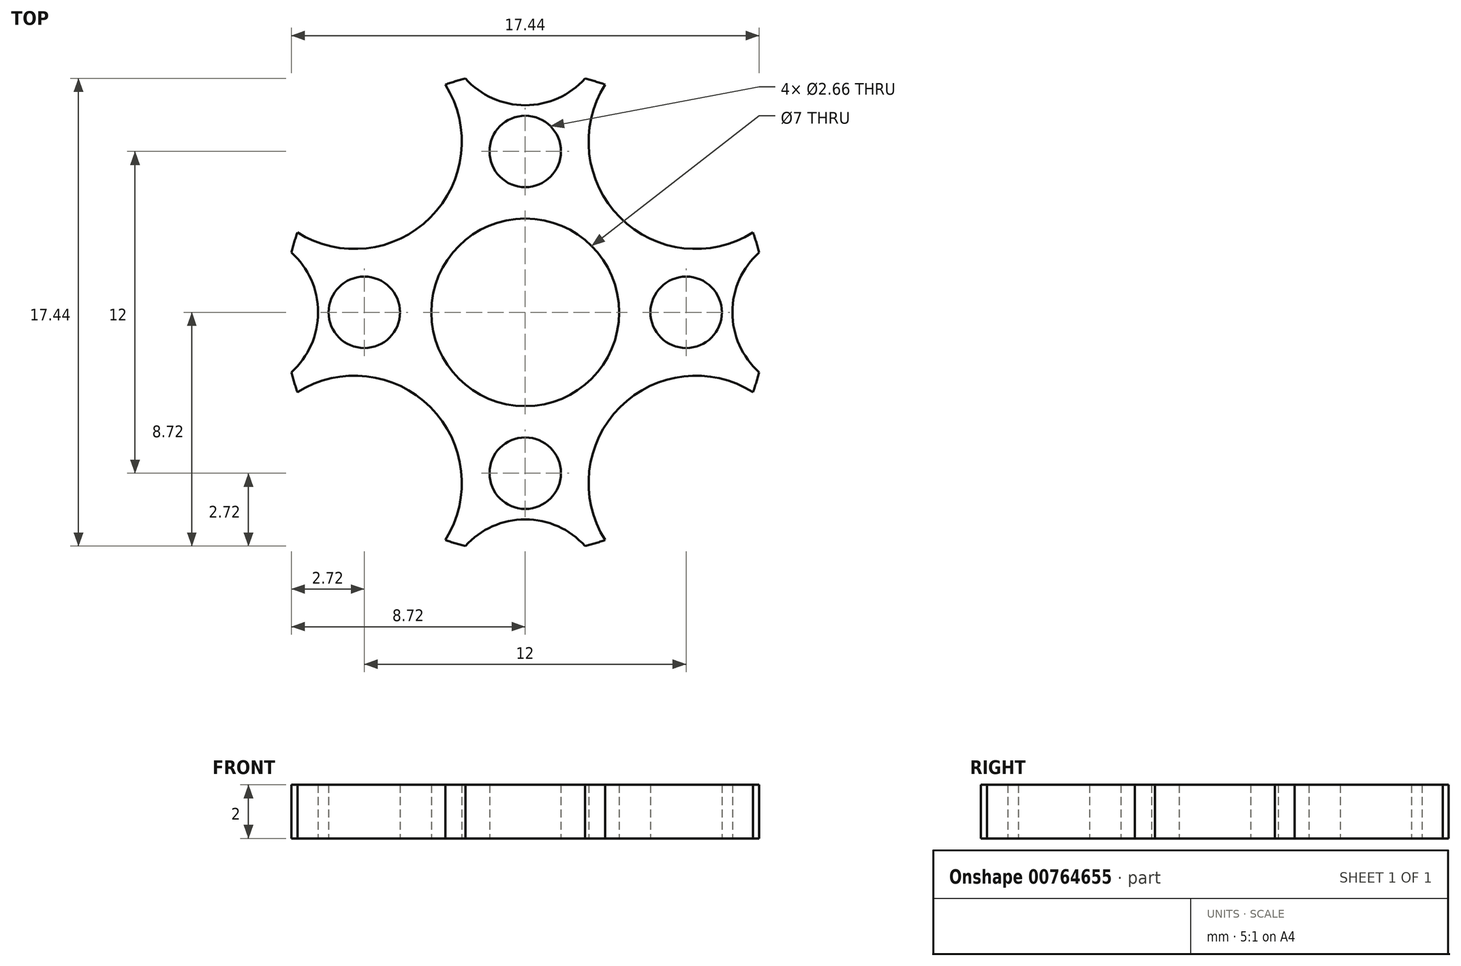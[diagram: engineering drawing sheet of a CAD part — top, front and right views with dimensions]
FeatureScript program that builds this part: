
annotation { "Feature Type Name" : "Feature", "Feature Type Description" : "" }
export const myFeature = defineFeature(function(context is Context, id is Id, definition is map)
    precondition{}
    {
        {
            var Q0;
            Q0=qCreatedBy(makeId("Top.planeOp"),FACE);
            var sketch = newSketch(context, id + "F0", { "sketchPlane" : qUnion([Q0])});
            skArc(sketch, "E0", {"start": v(-2.98, -8.5) * mm, "mid": v(-2.6, -8.61) * mm, "end": v(-2.23, -8.72) * mm});
            skCircle(sketch, "E1", {"center": v(0, 6) * mm, "radius": 1.33 * mm});
            skCircle(sketch, "E2.1.0", {"center": v(-6, 0) * mm, "radius": 1.33 * mm});
            skCircle(sketch, "E2.2.0", {"center": v(0, -6) * mm, "radius": 1.33 * mm});
            skCircle(sketch, "E2.3.0", {"center": v(6, 0) * mm, "radius": 1.33 * mm});
            skLineSegment(sketch, "E3", {"start": v(0, 0) * mm, "end": v(12.02, 12.02) * mm, "construction": true});
            skArc(sketch, "E4", {"start": v(2.98, 8.5) * mm, "mid": v(6.81, 2.39) * mm, "end": v(9.2, 9.2) * mm});
            skArc(sketch, "E5.1.0", {"start": v(-8.5, 2.98) * mm, "mid": v(-3.54, 3.54) * mm, "end": v(-2.98, 8.5) * mm});
            skArc(sketch, "E5.2.0", {"start": v(-2.98, -8.5) * mm, "mid": v(-3.54, -3.54) * mm, "end": v(-8.5, -2.98) * mm});
            skArc(sketch, "E5.3.0", {"start": v(8.5, -2.98) * mm, "mid": v(3.54, -3.54) * mm, "end": v(2.98, -8.5) * mm});
            skArc(sketch, "E6.trimOffspring", {"start": v(-8.5, 2.98) * mm, "mid": v(-8.61, 2.6) * mm, "end": v(-8.72, 2.23) * mm});
            skArc(sketch, "E7.trimOffspring", {"start": v(2.98, 8.5) * mm, "mid": v(2.6, 8.61) * mm, "end": v(2.23, 8.72) * mm});
            skArc(sketch, "E8.trimOffspring", {"start": v(8.5, -2.98) * mm, "mid": v(8.61, -2.6) * mm, "end": v(8.72, -2.23) * mm});
            skCircle(sketch, "E9", {"center": v(0, 0) * mm, "radius": 3.5 * mm});
            skArc(sketch, "E10", {"start": v(-2.23, 8.72) * mm, "mid": v(0, 7.72) * mm, "end": v(2.23, 8.72) * mm});
            skArc(sketch, "E11.1.0", {"start": v(-8.72, -2.23) * mm, "mid": v(-7.72, 0) * mm, "end": v(-8.72, 2.23) * mm});
            skArc(sketch, "E11.2.0", {"start": v(2.23, -8.72) * mm, "mid": v(0, -7.72) * mm, "end": v(-2.23, -8.72) * mm});
            skArc(sketch, "E11.3.0", {"start": v(8.72, 2.23) * mm, "mid": v(7.72, 0) * mm, "end": v(8.72, -2.23) * mm});
            skArc(sketch, "E12.trimOffspring", {"start": v(-8.72, -2.23) * mm, "mid": v(-8.61, -2.6) * mm, "end": v(-8.5, -2.98) * mm});
            skArc(sketch, "E13.trimOffspring", {"start": v(2.23, -8.72) * mm, "mid": v(2.6, -8.61) * mm, "end": v(2.98, -8.5) * mm});
            skArc(sketch, "E14.trimOffspring", {"start": v(8.72, 2.23) * mm, "mid": v(8.61, 2.6) * mm, "end": v(8.5, 2.98) * mm});
            skArc(sketch, "E15.trimOffspring", {"start": v(-2.23, 8.72) * mm, "mid": v(-2.6, 8.61) * mm, "end": v(-2.98, 8.5) * mm});
            skSolve(sketch);
        }
        {
            var Q0;
            Q0=makeQuery(id+"F0.imprint","IMPRINT",FACE,{"disambiguationData":[TD([[makeQuery(id+"F0.imprint","IMPRINT",EDGE,{"derivedFrom":sQuery(id+"F0.wireOp",EDGE,"E0")}),1.0]])]});
            extrude(context, id + "F1", {"entities" : qUnion([Q0]), "depth" : 2 * mm, "offsetDistance" : 25 * mm});
        }
    });
